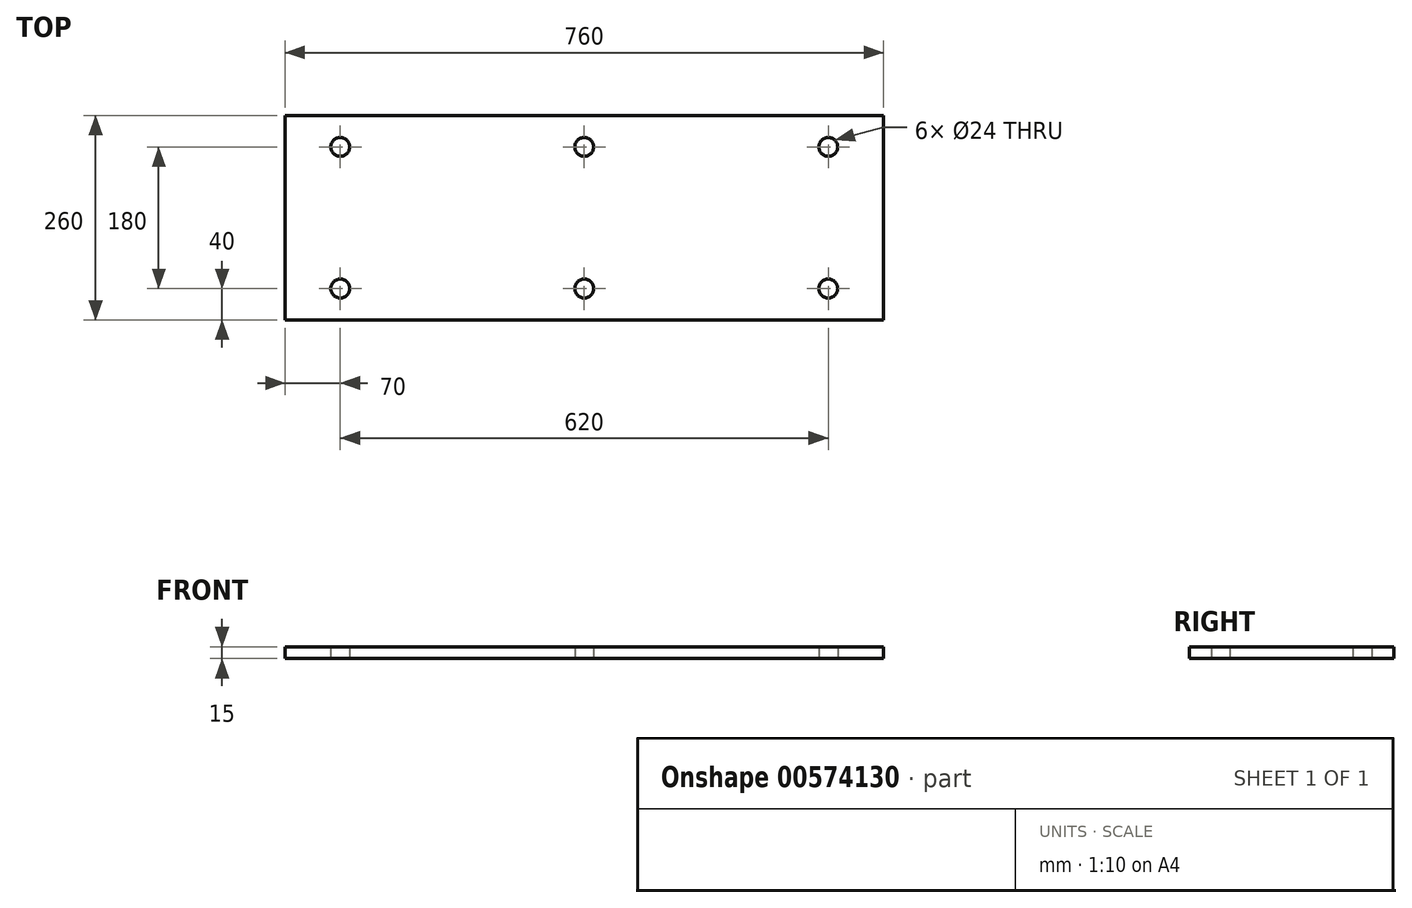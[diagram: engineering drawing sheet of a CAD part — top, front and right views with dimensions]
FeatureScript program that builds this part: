
annotation { "Feature Type Name" : "Feature", "Feature Type Description" : "" }
export const myFeature = defineFeature(function(context is Context, id is Id, definition is map)
    precondition{}
    {
        {
            var Q0;
            Q0=qCreatedBy(makeId("Top.planeOp"),FACE);
            var sketch = newSketch(context, id + "F0", { "sketchPlane" : qUnion([Q0])});
            skLineSegment(sketch, "E0.bottom", {"start": v(-380, 130) * mm, "end": v(380, 130) * mm});
            skLineSegment(sketch, "E0.top", {"start": v(-380, -130) * mm, "end": v(380, -130) * mm});
            skLineSegment(sketch, "E0.left", {"start": v(-380, 130) * mm, "end": v(-380, -130) * mm});
            skLineSegment(sketch, "E0.right", {"start": v(380, 130) * mm, "end": v(380, -130) * mm});
            skLineSegment(sketch, "E1", {"start": v(-380, 90) * mm, "end": v(380, 90) * mm, "construction": true});
            skLineSegment(sketch, "E2", {"start": v(-380, -90) * mm, "end": v(380, -90) * mm, "construction": true});
            skCircle(sketch, "E3", {"center": v(-310, 90) * mm, "radius": 12 * mm});
            skCircle(sketch, "E4", {"center": v(0, 90) * mm, "radius": 12 * mm});
            skCircle(sketch, "E5", {"center": v(310, 90) * mm, "radius": 12 * mm});
            skCircle(sketch, "E6", {"center": v(310, -90) * mm, "radius": 12 * mm});
            skCircle(sketch, "E7", {"center": v(0, -90) * mm, "radius": 12 * mm});
            skCircle(sketch, "E8", {"center": v(-310, -90) * mm, "radius": 12 * mm});
            skSolve(sketch);
        }
        {
            var Q0;
            Q0=makeQuery(id+"F0.imprint","IMPRINT",FACE,{"disambiguationData":[TD([[makeQuery(id+"F0.imprint","IMPRINT",EDGE,{"derivedFrom":sQuery(id+"F0.wireOp",EDGE,"E0.bottom")}),-1.0]])]});
            extrude(context, id + "F1", {"entities" : qUnion([Q0]), "depth" : 15 * mm, "offsetDistance" : 25 * mm});
        }
    });
